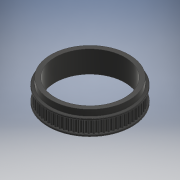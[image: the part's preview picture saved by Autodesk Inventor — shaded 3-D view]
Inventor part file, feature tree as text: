
AUTODESK INVENTOR PART (.ipt)
format: ipt  version: 2018 (Build 220112000, 112)  size: 717,312 bytes
history: native  units: mm
features: extrude x6, sketch x5, other x1, pattern_circular x1, fillet x1
ambient origin geometry x8: Origin, YZ Plane, XZ Plane, XY Plane, X Axis, Y Axis, Z Axis, Center Point
bodies: Solid1 (feature_tree)
feature tree (14):
  other  "Tooth"
  extrude  "Gear Solid Extrusion"  Depth=1.5mm
  extrude  "Tooth Cut-Out Extrusion"  Depth=0.85mm
  pattern_circular  "Teeth Array"  [2 undecoded]
  extrude  "Flange Extrusion Front"  Depth=10.0mm TaperAngle=0.0deg
  extrude  "Flange Extrusion Back"  Depth=5.0mm
  fillet  "Flange Fillet"  [1 undecoded]
  extrude  "Boss Extrusion"  Depth=34.422538mm
  extrude  "Bore Extrusion"  TaperAngle=0.0deg  [1 undecoded]
  sketch  "Sketch2"  dims[d2=33.422538mm d3=1.5mm]
  sketch  "Sketch3"  dims[d4=1.14mm d5=0.85mm]
  sketch  "Sketch4"  dims[d6=0.61mm]
  sketch  "Sketch5"  dims[d7=0.25mm]
  sketch  "Sketch6"  dims[d8=2.0mm d11=0.0mm d12=10.0mm d13=0.0mm d14=700.0mm d15=360.0deg d17=34.422538mm d19=0.0mm d20=34.422538mm d21=1.5mm d22=0.0mm d23=0.25mm d26=32.1mm d27=5.0mm d28=0.0mm d29=28.6mm d30=5.0mm d31=0.0mm]
note: 4 required parameter values undecoded (feature->parameter linkage not recoverable at this tier; creation-order binding heuristic only, values carry confidence <= 0.55)
